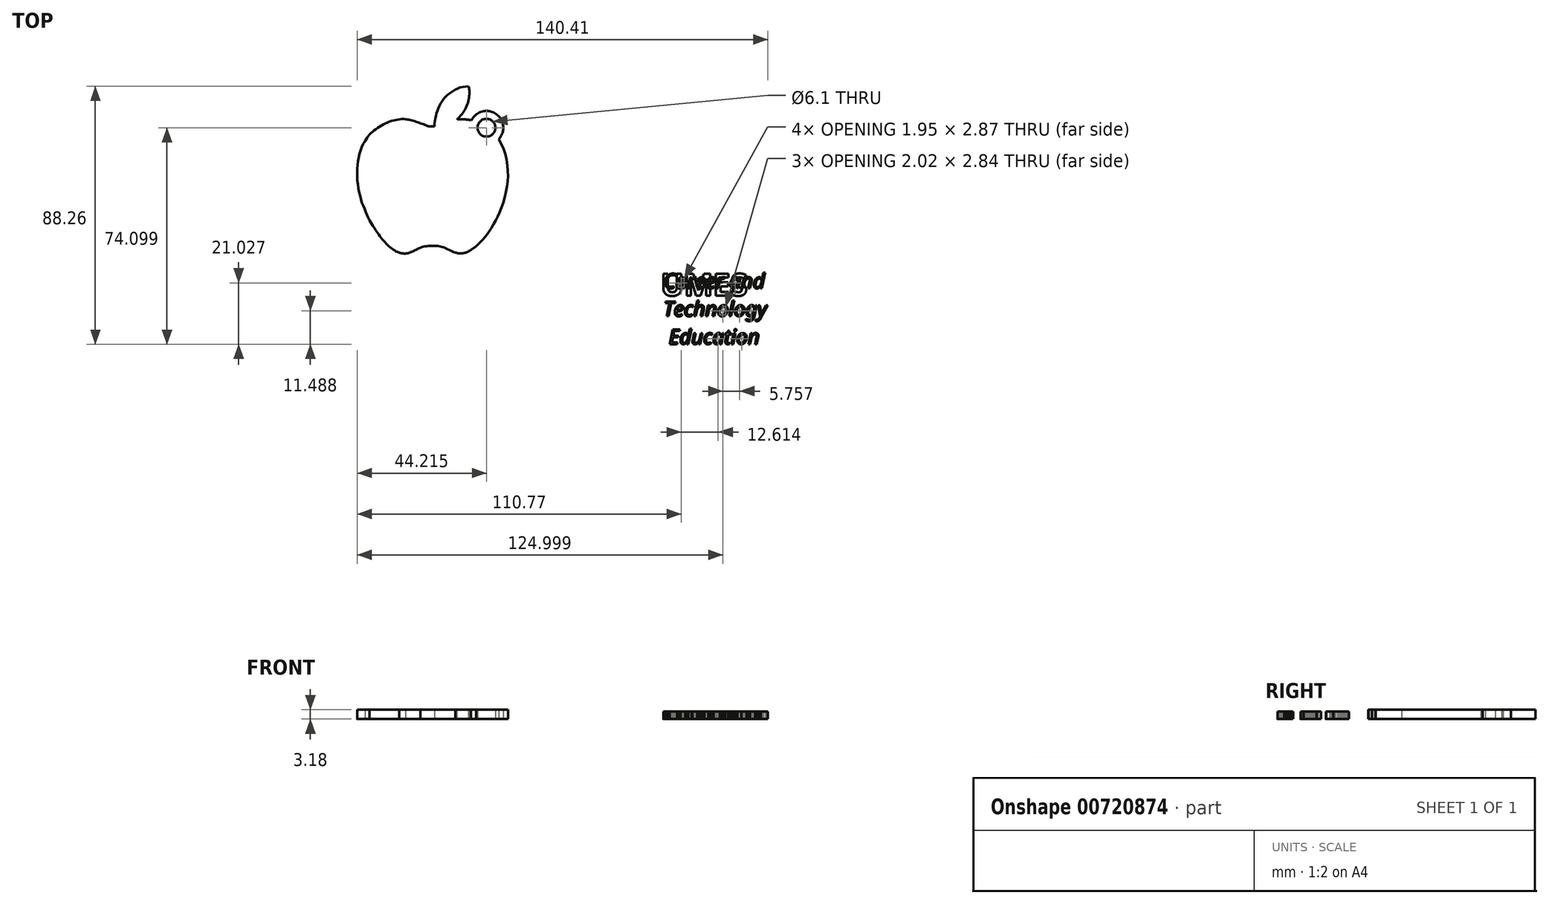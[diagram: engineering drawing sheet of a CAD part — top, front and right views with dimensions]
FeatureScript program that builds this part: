
annotation { "Feature Type Name" : "Feature", "Feature Type Description" : "" }
export const myFeature = defineFeature(function(context is Context, id is Id, definition is map)
    precondition{}
    {
        {
            var Q0;
            Q0=qCreatedBy(makeId("Top.planeOp"),FACE);
            var sketch = newSketch(context, id + "F0", { "sketchPlane" : qUnion([Q0])});
            skCircle(sketch, "E0", {"center": v(-59.53, 49.89) * mm, "radius": 3.05 * mm});
            skArc(sketch, "E1", {"start": v(-55.39, 45.93) * mm, "mid": v(-56.24, 54.59) * mm, "end": v(-64.67, 52.43) * mm});
            skFitSpline(sketch, "E2", {"points": [v(-64.67, 52.43) * mm, v(-69.66, 52.66) * mm, v(-71.93, 51.25) * mm], "startDerivative": vector(-9.59, 1.47) * mm, "endDerivative": vector(-4.68, -4.12) * mm});
            skFitSpline(sketch, "E3", {"points": [v(-69.66, 52.66) * mm, v(-66.9, 56.02) * mm, v(-65.54, 59.96) * mm, v(-65.4, 62.82) * mm, v(-65.72, 64.05) * mm], "startDerivative": vector(10.2, 10.54) * mm, "endDerivative": vector(-2.35, 6.78) * mm});
            skFitSpline(sketch, "E4", {"points": [v(-65.72, 64.05) * mm, v(-68.98, 63.5) * mm, v(-71.84, 61.82) * mm, v(-74.02, 60) * mm, v(-75.65, 57.33) * mm, v(-76.7, 54.52) * mm, v(-77.24, 51.57) * mm, v(-77.33, 50.3) * mm], "startDerivative": vector(-21.52, -1.58) * mm, "endDerivative": vector(-0.5, -11.65) * mm});
            skFitSpline(sketch, "E5", {"points": [v(-55.39, 45.93) * mm, v(-53.32, 41.64) * mm, v(-52.33, 36.83) * mm, v(-52.25, 32.55) * mm, v(-52.86, 27.98) * mm, v(-54.08, 23.47) * mm, v(-55.53, 19.81) * mm, v(-56.76, 17.52) * mm, v(-58.66, 14.32) * mm, v(-61.1, 11.26) * mm, v(-63.03, 9.37) * mm], "startDerivative": vector(20.95, -37.89) * mm, "endDerivative": vector(-22.74, -21.29) * mm});
            skFitSpline(sketch, "E6", {"points": [v(-77.33, 50.3) * mm, v(-78.34, 50.3) * mm, v(-79, 50.3) * mm, v(-80.29, 50.74) * mm, v(-82.2, 51.46) * mm, v(-84.15, 52.11) * mm, v(-86.09, 52.63) * mm, v(-87.15, 52.8) * mm], "startDerivative": vector(-8.93, 0.19) * mm, "endDerivative": vector(-7.8, 1.04) * mm});
            skFitSpline(sketch, "E7", {"points": [v(-101.1, 45.32) * mm, v(-100.2, 46.7) * mm, v(-99.27, 47.73) * mm, v(-98.15, 48.76) * mm, v(-96.8, 49.81) * mm, v(-95.2, 50.8) * mm, v(-93.47, 51.64) * mm, v(-91.57, 52.29) * mm, v(-90.06, 52.6) * mm, v(-88.52, 52.83) * mm, v(-87.15, 52.8) * mm], "startDerivative": vector(8.76, 14.5) * mm, "endDerivative": vector(14.81, -1) * mm});
            skFitSpline(sketch, "E8", {"points": [v(-101.1, 45.32) * mm, v(-101.75, 44.24) * mm, v(-102.36, 42.8) * mm, v(-102.82, 41.3) * mm, v(-103.27, 39.67) * mm, v(-103.54, 37.87) * mm, v(-103.73, 36.2) * mm, v(-103.73, 34.25) * mm, v(-103.73, 32.5) * mm, v(-103.52, 30.7) * mm, v(-103.21, 28.58) * mm, v(-102.83, 26.87) * mm, v(-102.4, 25.42) * mm, v(-102.07, 24.05) * mm, v(-101.5, 22.75) * mm, v(-100.84, 21.22) * mm, v(-100.41, 20.18) * mm, v(-100.06, 19.34) * mm, v(-99.47, 18.24) * mm], "startDerivative": vector(-13.27, -20.53) * mm, "endDerivative": vector(12.8, -22.8) * mm});
            skFitSpline(sketch, "E9", {"points": [v(-99.47, 18.24) * mm, v(-98.54, 16.65) * mm, v(-97.38, 14.75) * mm, v(-96.55, 13.57) * mm, v(-95.62, 12.25) * mm, v(-94.5, 10.97) * mm, v(-93.44, 9.81) * mm, v(-92.44, 8.98) * mm, v(-91.35, 8.2) * mm, v(-90.45, 7.6) * mm, v(-89.4, 7.18) * mm], "startDerivative": vector(8.04, -13.82) * mm, "endDerivative": vector(12.7, -4.22) * mm});
            skFitSpline(sketch, "E10", {"points": [v(-89.4, 7.18) * mm, v(-88.6, 6.95) * mm, v(-87.72, 6.85) * mm, v(-86.76, 6.9) * mm, v(-85.75, 7.18) * mm, v(-84.52, 7.67) * mm, v(-83.34, 8.3) * mm, v(-82.1, 8.85) * mm], "startDerivative": vector(6.26, -2.17) * mm, "endDerivative": vector(8.03, 3.6) * mm});
            skFitSpline(sketch, "E11", {"points": [v(-82.1, 8.85) * mm, v(-81.18, 9.18) * mm, v(-80.27, 9.35) * mm, v(-79.35, 9.42) * mm, v(-78.35, 9.45) * mm, v(-77.1, 9.42) * mm, v(-76.37, 9.42) * mm, v(-75.5, 9.33) * mm, v(-74.67, 9.13) * mm, v(-73.87, 8.85) * mm, v(-73.18, 8.46) * mm, v(-72.14, 7.93) * mm, v(-71.2, 7.52) * mm, v(-70.12, 7.18) * mm], "startDerivative": vector(11.59, 4.14) * mm, "endDerivative": vector(13.32, -3.83) * mm});
            skFitSpline(sketch, "E12", {"points": [v(-70.12, 7.18) * mm, v(-69.26, 6.92) * mm, v(-68.37, 6.9) * mm, v(-67.4, 6.97) * mm, v(-65.97, 7.45) * mm, v(-64.88, 8.05) * mm], "startDerivative": vector(4.7, -1.76) * mm, "endDerivative": vector(4.74, 2.9) * mm});
            skFitSpline(sketch, "E13", {"points": [v(-64.88, 8.05) * mm, v(-64.02, 8.65) * mm, v(-63.03, 9.37) * mm], "startDerivative": vector(1.77, 1.22) * mm, "endDerivative": vector(1.94, 1.42) * mm});
            skSolve(sketch);
        }
        {
            var Q0;
            Q0=qCreatedBy(makeId("Top.planeOp"),FACE);
            var sketch = newSketch(context, id + "F1", { "sketchPlane" : qUnion([Q0])});
            skText(sketch, "E14", { "text": "UMES\n", "fontName": "NotoSans-Bold.ttf"});
            const initialGuessF1  = {"E14": [0, -0.0076, 1, 0, 0.0076]};
            skSetInitialGuess(sketch, initialGuessF1);
            skSolve(sketch);
        }
        {
            var Q0;
            Q0=makeQuery(id+"F0.imprint","IMPRINT",FACE,{"disambiguationData":[TD([[makeQuery(id+"F0.imprint","IMPRINT",EDGE,{"derivedFrom":sQuery(id+"F0.wireOp",EDGE,"E0")}),-1.0]])]});
            extrude(context, id + "F2", {"entities" : qUnion([Q0]), "depth" : 3.17 * mm, "offsetDistance" : 25.4 * mm});
        }
        {
            var Q0;
            Q0=qSketchRegion(id+"F1",true);
            extrude(context, id + "F3", {"entities" : qUnion([Q0]), "depth" : 2.54 * mm, "offsetDistance" : 25.4 * mm});
        }
        {
            var Q0;
            Q0=qCreatedBy(makeId("Top.planeOp"),FACE);
            var sketch = newSketch(context, id + "F4", { "sketchPlane" : qUnion([Q0])});
            skText(sketch, "E15", { "text": "Career and\nTechnology\n Education", "fontName": "NotoSans-Italic.ttf"});
            const initialGuessF4  = {"E15": [0.00096, -0.00506, 1, 0, 0.00505]};
            skSetInitialGuess(sketch, initialGuessF4);
            skSolve(sketch);
        }
        {
            var Q0;
            Q0=qSketchRegion(id+"F4",true);
            extrude(context, id + "F5", {"entities" : qUnion([Q0]), "depth" : 2.54 * mm, "offsetDistance" : 25.4 * mm});
        }
    });
